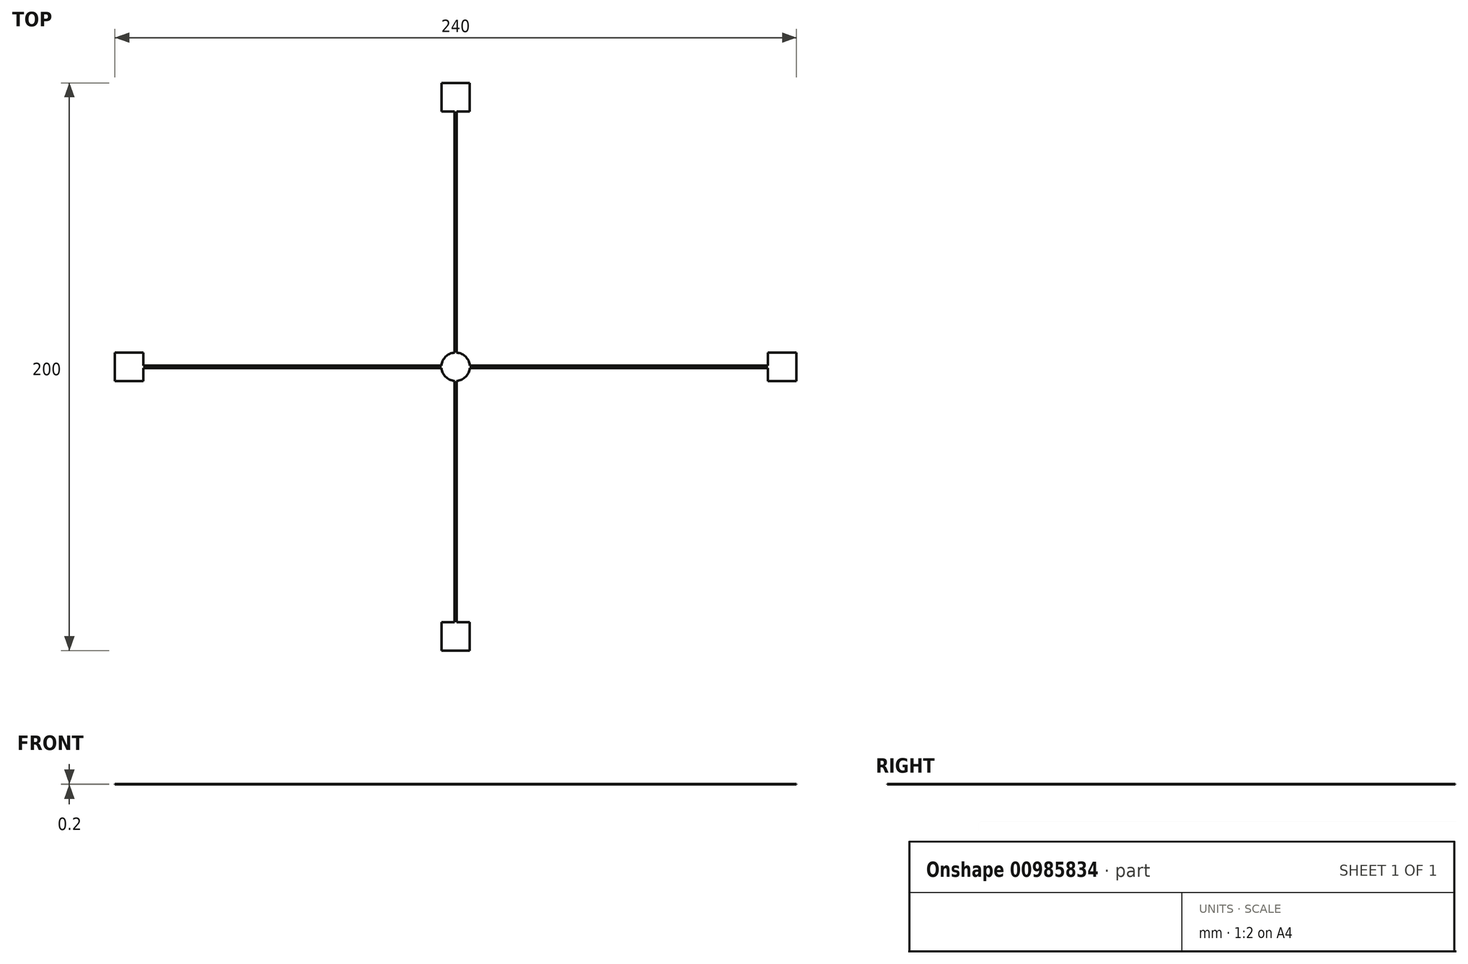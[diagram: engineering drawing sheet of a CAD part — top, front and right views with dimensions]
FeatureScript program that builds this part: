
annotation { "Feature Type Name" : "Feature", "Feature Type Description" : "" }
export const myFeature = defineFeature(function(context is Context, id is Id, definition is map)
    precondition{}
    {
        {
            var Q0;
            Q0=qCreatedBy(makeId("Top.planeOp"),FACE);
            var sketch = newSketch(context, id + "F0", { "sketchPlane" : qUnion([Q0])});
            skCircle(sketch, "E0", {"center": v(0, 0) * mm, "radius": 5 * mm});
            skLineSegment(sketch, "E1", {"start": v(0, 0) * mm, "end": v(-5, 0) * mm, "construction": true});
            skLineSegment(sketch, "E2", {"start": v(0, 0) * mm, "end": v(0, 5) * mm, "construction": true});
            skLineSegment(sketch, "E3", {"start": v(-5, 0) * mm, "end": v(-110, 0) * mm, "construction": true});
            skLineSegment(sketch, "E4", {"start": v(0, 5) * mm, "end": v(0, 100) * mm, "construction": true});
            skLineSegment(sketch, "E5", {"start": v(0, 0) * mm, "end": v(0, -5) * mm, "construction": true});
            skLineSegment(sketch, "E6", {"start": v(0, 0) * mm, "end": v(5, 0) * mm, "construction": true});
            skLineSegment(sketch, "E7", {"start": v(0, -5) * mm, "end": v(0, -100) * mm, "construction": true});
            skLineSegment(sketch, "E8", {"start": v(5, 0) * mm, "end": v(110, 0) * mm, "construction": true});
            skLineSegment(sketch, "E9.bottom", {"start": v(-120, 5) * mm, "end": v(-110, 5) * mm});
            skLineSegment(sketch, "E9.top", {"start": v(-120, -5) * mm, "end": v(-110, -5) * mm});
            skLineSegment(sketch, "E9.left", {"start": v(-110, 5) * mm, "end": v(-110, -5) * mm});
            skLineSegment(sketch, "E9.right", {"start": v(-120, 5) * mm, "end": v(-120, -5) * mm});
            skLineSegment(sketch, "E10", {"start": v(-120, 0) * mm, "end": v(-110, 0) * mm, "construction": true});
            skLineSegment(sketch, "E11", {"start": v(-115, 5) * mm, "end": v(-115, -5) * mm, "construction": true});
            skPoint(sketch, "E12", {"position": v(-115, 0) * mm});
            skLineSegment(sketch, "E13.bottom", {"start": v(-5, 100) * mm, "end": v(5, 100) * mm});
            skLineSegment(sketch, "E13.top", {"start": v(-5, 90) * mm, "end": v(5, 90) * mm});
            skLineSegment(sketch, "E13.left", {"start": v(-5, 100) * mm, "end": v(-5, 90) * mm});
            skLineSegment(sketch, "E13.right", {"start": v(5, 100) * mm, "end": v(5, 90) * mm});
            skLineSegment(sketch, "E14", {"start": v(-5, 95) * mm, "end": v(5, 95) * mm, "construction": true});
            skLineSegment(sketch, "E15", {"start": v(0, 100) * mm, "end": v(0, 90) * mm, "construction": true});
            skPoint(sketch, "E16", {"position": v(0, 95) * mm});
            skLineSegment(sketch, "E17.bottom", {"start": v(110, 5) * mm, "end": v(120, 5) * mm});
            skLineSegment(sketch, "E17.top", {"start": v(110, -5) * mm, "end": v(120, -5) * mm});
            skLineSegment(sketch, "E17.left", {"start": v(120, 5) * mm, "end": v(120, -5) * mm});
            skLineSegment(sketch, "E17.right", {"start": v(110, 5) * mm, "end": v(110, -5) * mm});
            skLineSegment(sketch, "E18", {"start": v(110, 0) * mm, "end": v(120, 0) * mm, "construction": true});
            skLineSegment(sketch, "E19", {"start": v(115, 5) * mm, "end": v(115, -5) * mm, "construction": true});
            skPoint(sketch, "E20", {"position": v(115, 0) * mm});
            skLineSegment(sketch, "E21.bottom", {"start": v(-5, -90) * mm, "end": v(5, -90) * mm});
            skLineSegment(sketch, "E21.top", {"start": v(-5, -100) * mm, "end": v(5, -100) * mm});
            skLineSegment(sketch, "E21.left", {"start": v(-5, -90) * mm, "end": v(-5, -100) * mm});
            skLineSegment(sketch, "E21.right", {"start": v(5, -90) * mm, "end": v(5, -100) * mm});
            skLineSegment(sketch, "E22", {"start": v(-5, -95) * mm, "end": v(5, -95) * mm, "construction": true});
            skLineSegment(sketch, "E23", {"start": v(0, -90) * mm, "end": v(0, -100) * mm, "construction": true});
            skPoint(sketch, "E24", {"position": v(0, -95) * mm});
            skLineSegment(sketch, "E25", {"start": v(-4.98, 0.43) * mm, "end": v(-110, 0.43) * mm});
            skLineSegment(sketch, "E26", {"start": v(-0.43, 4.98) * mm, "end": v(-0.43, 90) * mm});
            skLineSegment(sketch, "E27.MirrorCS", {"start": v(-4.98, -0.43) * mm, "end": v(-110, -0.43) * mm});
            skLineSegment(sketch, "E28.MirrorCS", {"start": v(0.43, 4.98) * mm, "end": v(0.43, 90) * mm});
            skLineSegment(sketch, "E29", {"start": v(4.98, 0.43) * mm, "end": v(110, 0.43) * mm});
            skLineSegment(sketch, "E30.MirrorCS", {"start": v(4.98, -0.43) * mm, "end": v(110, -0.43) * mm});
            skLineSegment(sketch, "E31", {"start": v(0.43, -4.98) * mm, "end": v(0.43, -90) * mm});
            skLineSegment(sketch, "E32.MirrorCS", {"start": v(-0.43, -4.98) * mm, "end": v(-0.43, -90) * mm});
            skLineSegment(sketch, "E33", {"start": v(-57.5, 0.43) * mm, "end": v(-57.5, -0.43) * mm, "construction": true});
            skLineSegment(sketch, "E34", {"start": v(-0.43, 47.5) * mm, "end": v(0.43, 47.5) * mm, "construction": true});
            skLineSegment(sketch, "E35", {"start": v(57.5, 0.43) * mm, "end": v(57.5, -0.43) * mm, "construction": true});
            skLineSegment(sketch, "E36", {"start": v(0.43, -47.5) * mm, "end": v(-0.43, -47.5) * mm, "construction": true});
            skSolve(sketch);
        }
        {
            var Q0;
            {var subQ3=sQuery(id+"F0.wireOp",EDGE,"E9.bottom");Q0=makeQuery(id+"F0.imprint","IMPRINT",FACE,{"disambiguationData":[TD([[makeQuery(id+"F0.imprint","IMPRINT",EDGE,{"derivedFrom":subQ3}),-1.0]])]});}
            var Q1;
            {var subQ0=sQuery(id+"F0.wireOp",EDGE,"E25");Q1=makeQuery(id+"F0.imprint","IMPRINT",FACE,{"disambiguationData":[TD([[makeQuery(id+"F0.imprint","IMPRINT",EDGE,{"derivedFrom":subQ0}),1.0]])]});}
            var Q2;
            {var subQ0=sQuery(id+"F0.wireOp",EDGE,"WEkQUdyM-sZYD-53Kn-fVou-AGer5MQ2EUuG");Q2=makeQuery(id+"F0.imprint","IMPRINT",FACE,{"disambiguationData":[TD([[makeQuery(id+"F0.imprint","IMPRINT",EDGE,{"derivedFrom":subQ0}),-1.0]])]});}
            var Q3;
            {var subQ0=sQuery(id+"F0.wireOp",EDGE,"E26");Q3=makeQuery(id+"F0.imprint","IMPRINT",FACE,{"disambiguationData":[TD([[makeQuery(id+"F0.imprint","IMPRINT",EDGE,{"derivedFrom":subQ0}),-1.0]])]});}
            var Q4;
            {var subQ0=sQuery(id+"F0.wireOp",EDGE,"E29");Q4=makeQuery(id+"F0.imprint","IMPRINT",FACE,{"disambiguationData":[TD([[makeQuery(id+"F0.imprint","IMPRINT",EDGE,{"derivedFrom":subQ0}),-1.0]])]});}
            var Q5;
            Q5=makeQuery(id+"F0.imprint","IMPRINT",FACE,{"disambiguationData":[TD([[makeQuery(id+"F0.imprint","IMPRINT",EDGE,{"derivedFrom":sQuery(id+"F0.wireOp",EDGE,"ly7hbJHH-pp2l-Vwt9-JZXV-C165xYYjUS7a")}),-1.0]])]});
            var Q6;
            Q6=makeQuery(id+"F0.imprint","IMPRINT",FACE,{"disambiguationData":[TD([[makeQuery(id+"F0.imprint","IMPRINT",EDGE,{"derivedFrom":sQuery(id+"F0.wireOp",EDGE,"8fOBDVqu-Kbux-AQQc-SsKX-zmi1PV7WOsuc")}),-1.0]])]});
            var Q7;
            {var subQ0=sQuery(id+"F0.wireOp",EDGE,"j68Ea4Af-Guzo-vbPW-3NuJ-hjVbAdSlOdlf");Q7=makeQuery(id+"F0.imprint","IMPRINT",FACE,{"disambiguationData":[TD([[makeQuery(id+"F0.imprint","IMPRINT",EDGE,{"derivedFrom":subQ0}),-1.0]])]});}
            var Q8;
            {var subQ0=sQuery(id+"F0.wireOp",EDGE,"zkSYKa9q-evII-kxpR-jHcW-q6WqRbUjRM8D");Q8=makeQuery(id+"F0.imprint","IMPRINT",FACE,{"disambiguationData":[TD([[makeQuery(id+"F0.imprint","IMPRINT",EDGE,{"derivedFrom":subQ0}),-1.0]])]});}
            var Q9;
            {var subQ0=sQuery(id+"F0.wireOp",EDGE,"ckprx1UK-Nf1c-fZhx-13kz-Vn1D3q1Eh76r");Q9=makeQuery(id+"F0.imprint","IMPRINT",FACE,{"disambiguationData":[TD([[makeQuery(id+"F0.imprint","IMPRINT",EDGE,{"derivedFrom":subQ0}),-1.0]])]});}
            var Q10;
            Q10=makeQuery(id+"F0.imprint","IMPRINT",FACE,{"disambiguationData":[TD([[makeQuery(id+"F0.imprint","IMPRINT",EDGE,{"derivedFrom":sQuery(id+"F0.wireOp",EDGE,"Wf9HyLDT-unUe-Yyc4-iVRE-nW4IGXZqaAKb")}),-1.0]])]});
            var Q11;
            Q11=makeQuery(id+"F0.imprint","IMPRINT",FACE,{"disambiguationData":[TD([[makeQuery(id+"F0.imprint","IMPRINT",EDGE,{"derivedFrom":sQuery(id+"F0.wireOp",EDGE,"BZ57VupH-gWfJ-GeMK-ACLr-HJ0cDJAKZmvk")}),-1.0]])]});
            var Q12;
            {var subQ0=sQuery(id+"F0.wireOp",EDGE,"E31");Q12=makeQuery(id+"F0.imprint","IMPRINT",FACE,{"disambiguationData":[TD([[makeQuery(id+"F0.imprint","IMPRINT",EDGE,{"derivedFrom":subQ0}),-1.0]])]});}
            var Q13;
            {var subQ1=sQuery(id+"F0.wireOp",EDGE,"E17.bottom");Q13=makeQuery(id+"F0.imprint","IMPRINT",FACE,{"disambiguationData":[TD([[makeQuery(id+"F0.imprint","IMPRINT",EDGE,{"derivedFrom":subQ1}),-1.0]])]});}
            var Q14;
            Q14=makeQuery(id+"F0.imprint","IMPRINT",FACE,{"disambiguationData":[TD([[makeQuery(id+"F0.imprint","IMPRINT",EDGE,{"derivedFrom":sQuery(id+"F0.wireOp",EDGE,"E21.top")}),1.0]])]});
            var Q15;
            Q15=makeQuery(id+"F0.imprint","IMPRINT",FACE,{"disambiguationData":[TD([[makeQuery(id+"F0.imprint","IMPRINT",EDGE,{"derivedFrom":sQuery(id+"F0.wireOp",EDGE,"E13.bottom")}),-1.0]])]});
            var Q16;
            {var subQ0=sQuery(id+"F0.wireOp",EDGE,"E0");var subQ8=makeQuery(id+"F0.imprint","INTERSECT",VERTEX,{"derivedFrom":[subQ0,sQuery(id+"F0.wireOp",EDGE,"E29")]});Q16=makeQuery(id+"F0.imprint","IMPRINT",FACE,{"disambiguationData":[TD([[makeQuery(id+"F0.imprint","IMPRINT",EDGE,{"disambiguationData":[TD([[subQ8,-1.0]])],"derivedFrom":subQ0}),1.0]])]});}
            extrude(context, id + "F1", {"entities" : qUnion([Q0, Q1, Q2, Q3, Q4, Q5, Q6, Q7, Q8, Q9, Q10, Q11, Q12, Q13, Q14, Q15, Q16]), "depth" : .2 * mm, "offsetDistance" : 25 * mm});
        }
    });
